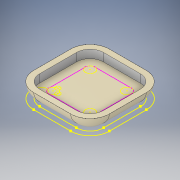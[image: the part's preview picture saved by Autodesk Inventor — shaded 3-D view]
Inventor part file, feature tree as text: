
AUTODESK INVENTOR PART (.ipt)
format: ipt  version: 2018 (Build 220112000, 112)  size: 304,128 bytes
history: native  units: in
note: dims shown in document units (in); Inventor stores cm internally (conversion verified against a paired STEP export)
features: other x6, extrude x1, projected_geometry x1
ambient origin geometry x8: Origin, YZ Plane, XZ Plane, XY Plane, X Axis, Y Axis, Z Axis, Center Point
bodies: Solid1 (feature_tree)
feature tree (8):
  other  "Case Bottom.ipt"
  extrude  "Narrowing Extrusion"  Depth=0.3937in
  other  "Solid2::Case Bottom.ipt"
  other  "TaggingFeature1"
  other  "Alignment Sketch"
  other  "Peg Sketch"
  other  "Narrowing Sketch"
  projected_geometry  "Projected Loop1"
